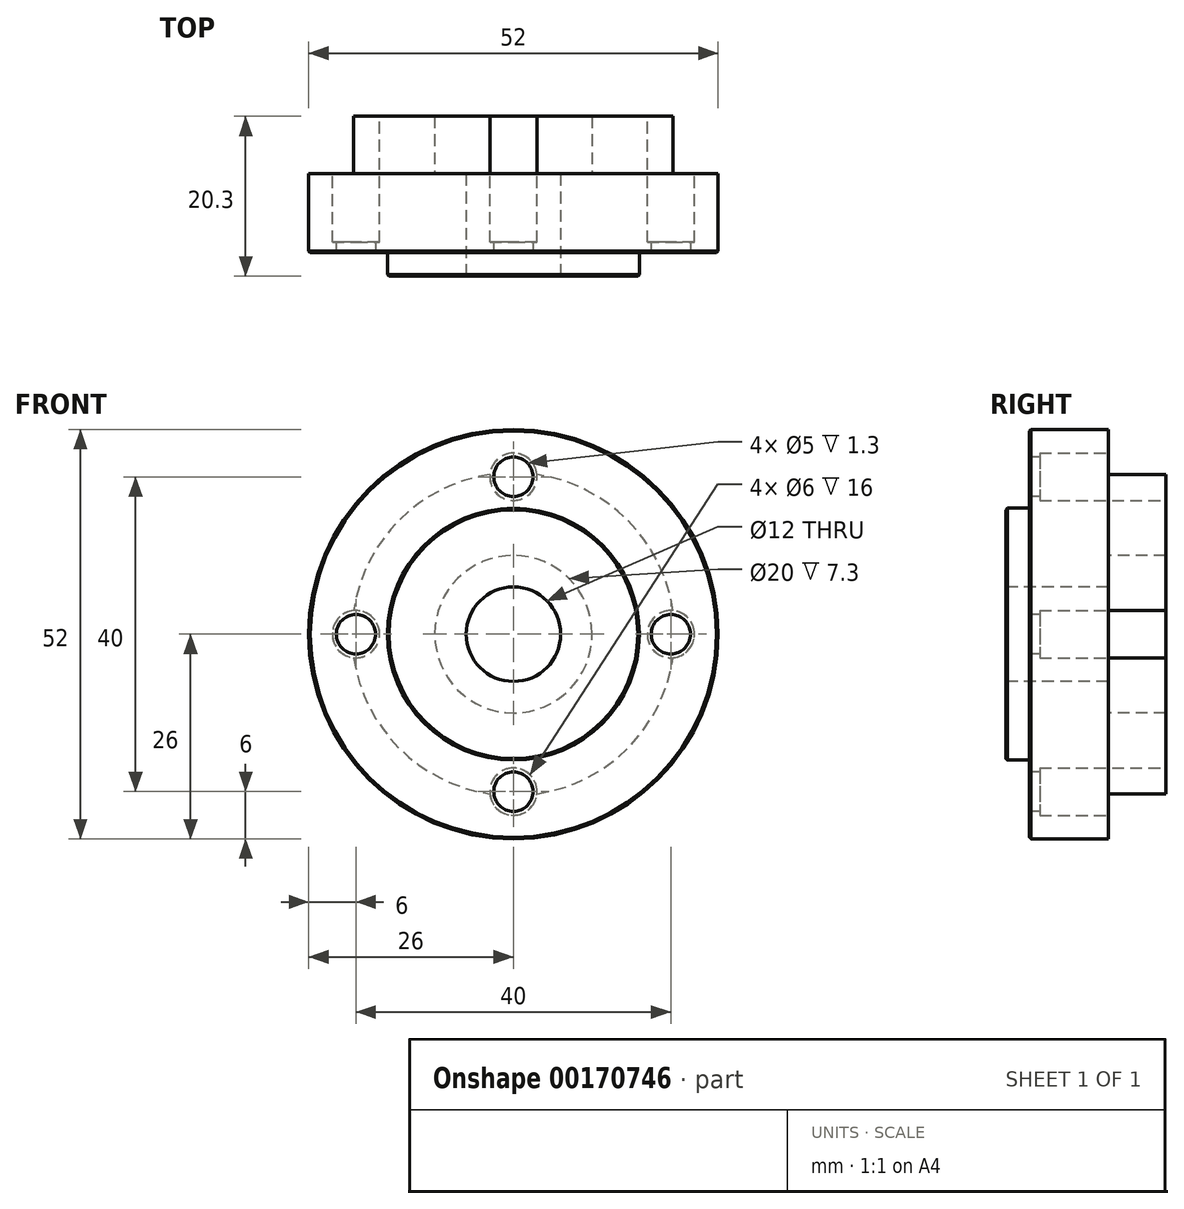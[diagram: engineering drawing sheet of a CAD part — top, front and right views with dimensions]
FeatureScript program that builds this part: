
annotation { "Feature Type Name" : "Feature", "Feature Type Description" : "" }
export const myFeature = defineFeature(function(context is Context, id is Id, definition is map)
    precondition{}
    {
        {
            var Q0;
            Q0=qCreatedBy(makeId("Front.planeOp"),FACE);
            var sketch = newSketch(context, id + "F0", { "sketchPlane" : qUnion([Q0])});
            skCircle(sketch, "E0", {"center": v(0, 0) * mm, "radius": 26 * mm});
            skLineSegment(sketch, "E1", {"start": v(0, 21.9) * mm, "end": v(0, -21.86) * mm, "construction": true});
            skLineSegment(sketch, "E2", {"start": v(-20.2, 0) * mm, "end": v(21.4, 0) * mm, "construction": true});
            skCircle(sketch, "E3", {"center": v(0, 0) * mm, "radius": 20 * mm, "construction": true});
            skCircle(sketch, "E4", {"center": v(0, 20) * mm, "radius": 2.5 * mm});
            skCircle(sketch, "E5.1.0", {"center": v(-20, 0) * mm, "radius": 2.5 * mm});
            skCircle(sketch, "E5.2.0", {"center": v(0, -20) * mm, "radius": 2.5 * mm});
            skCircle(sketch, "E5.3.0", {"center": v(20, 0) * mm, "radius": 2.5 * mm});
            skCircle(sketch, "E6", {"center": v(0, 0) * mm, "radius": 6 * mm});
            skSolve(sketch);
        }
        {
            var Q0;
            Q0=qSketchRegion(id+"F0",true);
            extrude(context, id + "F1", {"entities" : qUnion([Q0]), "flatOperationType" : FlatOperationType.REMOVE, "oppositeDirection" : true, "offsetDistance" : 25 * mm, "depth" : 10 * mm, "domain" : OperationDomain.MODEL});
        }
        {
            var Q0;
            Q0=qCreatedBy(makeId("Front.planeOp"),FACE);
            var sketch = newSketch(context, id + "F2", { "sketchPlane" : qUnion([Q0])});
            skCircle(sketch, "E7", {"center": v(0, 0) * mm, "radius": 16 * mm});
            skCircle(sketch, "E8.0", {"center": v(0, 0) * mm, "radius": 6 * mm});
            skSolve(sketch);
        }
        {
            var Q0;
            Q0=qSketchRegion(id+"F2",true);
            extrude(context, id + "F3", {"entities" : qUnion([Q0]), "operationType" : NewBodyOperationType.ADD, "depth" : 3 * mm});
        }
        {
            var Q0;
            Q0=makeQuery(id+"F3.opExtrude","CAP_EDGE",EDGE,{"disambiguationData":[OSD([sQuery(id+"F2.wireOp",EDGE,"E7")])],"isStart":false});
            var Q1;
            Q1=makeQuery(id+"F1.opExtrude","CAP_EDGE",EDGE,{"disambiguationData":[OSD([sQuery(id+"F0.wireOp",EDGE,"E0")])],"isStart":true});
            chamfer(context, id + "F4", {"entities" : qUnion([Q0, Q1]), "width" : 0.2 * mm, "tangentPropagation" : true});
        }
        {
            var Q0;
            Q0=makeQuery(id+"F1.opExtrude","CAP_FACE",FACE,{"disambiguationData":[OSD([sQuery(id+"F0.wireOp",EDGE,"E0"),sQuery(id+"F0.wireOp",EDGE,"E4"),sQuery(id+"F0.wireOp",EDGE,"E5.1.0"),sQuery(id+"F0.wireOp",EDGE,"E5.2.0"),sQuery(id+"F0.wireOp",EDGE,"E5.3.0"),sQuery(id+"F0.wireOp",EDGE,"E6")])],"isStart":false});
            var sketch = newSketch(context, id + "F5", { "sketchPlane" : qUnion([Q0])});
            skCircle(sketch, "E9", {"center": v(0, 0) * mm, "radius": 10 * mm});
            skCircle(sketch, "E10", {"center": v(0, 0) * mm, "radius": 20.5 * mm});
            skSolve(sketch);
        }
        {
            var Q0;
            Q0=qSketchRegion(id+"F5",true);
            extrude(context, id + "F6", {"entities" : qUnion([Q0]), "operationType" : NewBodyOperationType.ADD, "flatOperationType" : FlatOperationType.REMOVE, "offsetDistance" : 25 * mm, "depth" : 7.3 * mm, "domain" : OperationDomain.MODEL});
        }
        {
            var Q0;
            Q0=makeQuery(id+"F6.opExtrude","CAP_FACE",FACE,{"disambiguationData":[OSD([sQuery(id+"F5.wireOp",EDGE,"E9"),sQuery(id+"F5.wireOp",EDGE,"E10")])],"isStart":false});
            var sketch = newSketch(context, id + "F7", { "sketchPlane" : qUnion([Q0])});
            skCircle(sketch, "E11.0", {"center": v(-20, 0) * mm, "radius": 2.5 * mm, "construction": true});
            skCircle(sketch, "E12.0", {"center": v(-20, 0) * mm, "radius": 3 * mm});
            skCircle(sketch, "E13.1.0", {"center": v(0, -20) * mm, "radius": 3 * mm});
            skCircle(sketch, "E13.2.0", {"center": v(20, 0) * mm, "radius": 3 * mm});
            skCircle(sketch, "E13.3.0", {"center": v(0, 20) * mm, "radius": 3 * mm});
            skPoint(sketch, "E13.center", {"position": v(0, 0) * mm});
            skSolve(sketch);
        }
        {
            var Q0;
            Q0=qSketchRegion(id+"F7",true);
            extrude(context, id + "F8", {"entities" : qUnion([Q0]), "operationType" : NewBodyOperationType.REMOVE, "oppositeDirection" : true, "depth" : 16 * mm});
        }
    });
